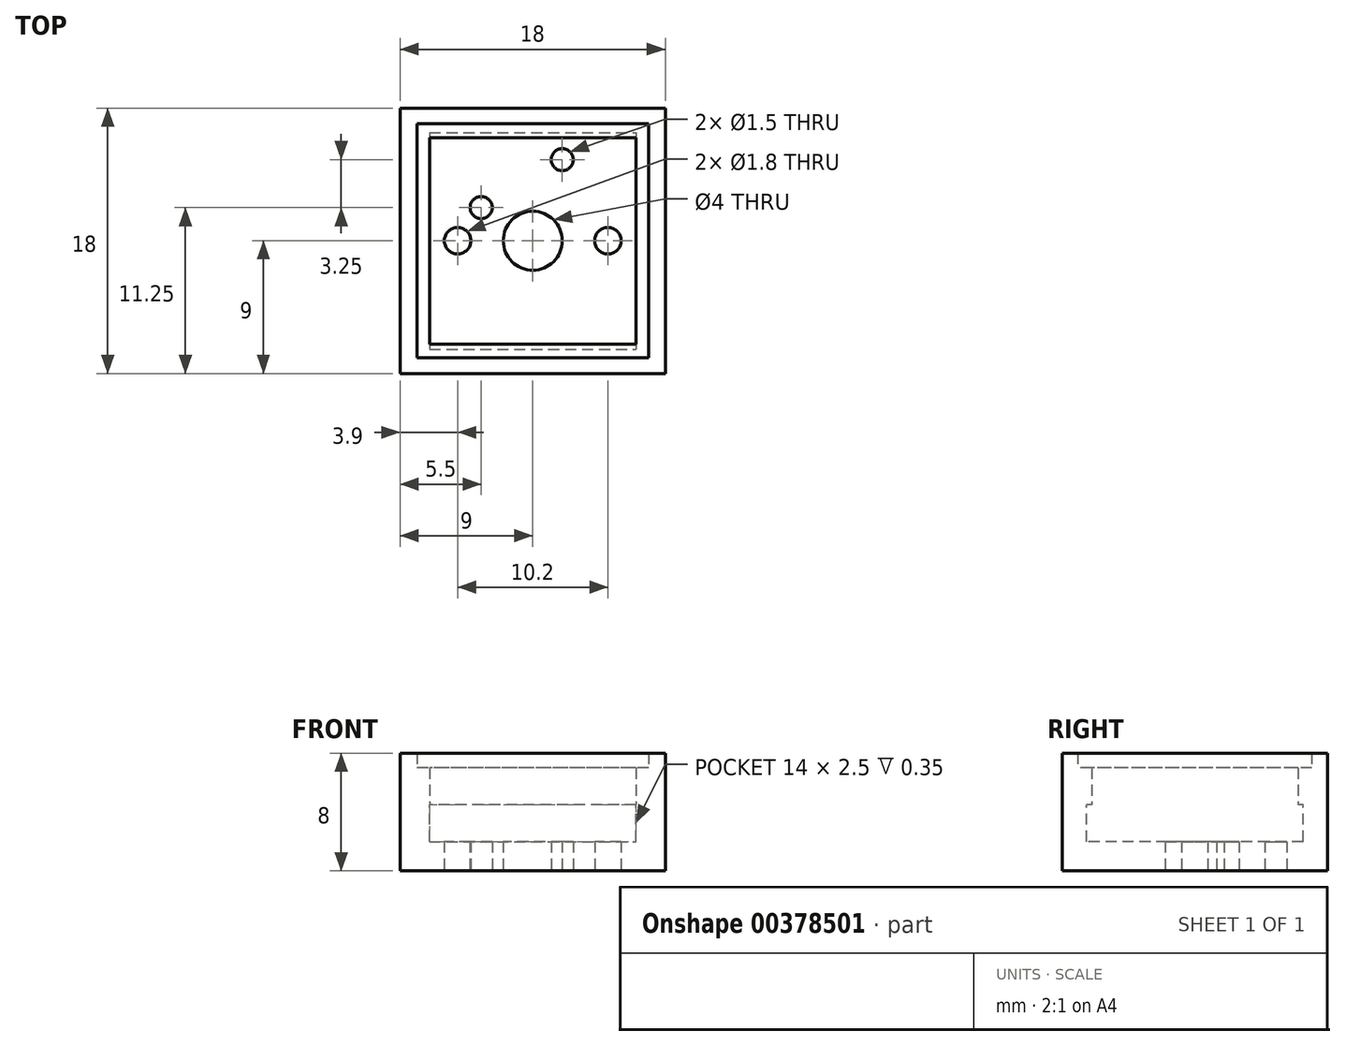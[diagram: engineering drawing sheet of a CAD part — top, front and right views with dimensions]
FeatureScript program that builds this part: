
annotation { "Feature Type Name" : "Feature", "Feature Type Description" : "" }
export const myFeature = defineFeature(function(context is Context, id is Id, definition is map)
    precondition{}
    {
        {
            var Q0;
            Q0=qCreatedBy(makeId("Top.planeOp"),FACE);
            var sketch = newSketch(context, id + "F0", { "sketchPlane" : qUnion([Q0])});
            skLineSegment(sketch, "E0.bottom", {"start": v(9, 9) * mm, "end": v(-9, 9) * mm});
            skLineSegment(sketch, "E0.top", {"start": v(9, -9) * mm, "end": v(-9, -9) * mm});
            skLineSegment(sketch, "E0.left", {"start": v(9, 9) * mm, "end": v(9, -9) * mm});
            skLineSegment(sketch, "E0.right", {"start": v(-9, 9) * mm, "end": v(-9, -9) * mm});
            skPoint(sketch, "E0.middle", {"position": v(0, 0) * mm});
            skLineSegment(sketch, "E1.bottom", {"start": v(7.85, 7.95) * mm, "end": v(-7.85, 7.95) * mm});
            skLineSegment(sketch, "E1.top", {"start": v(7.85, -7.95) * mm, "end": v(-7.85, -7.95) * mm});
            skLineSegment(sketch, "E1.left", {"start": v(7.85, 7.95) * mm, "end": v(7.85, -7.95) * mm});
            skLineSegment(sketch, "E1.right", {"start": v(-7.85, 7.95) * mm, "end": v(-7.85, -7.95) * mm});
            skLineSegment(sketch, "E2.bottom", {"start": v(7, 7) * mm, "end": v(-7, 7) * mm});
            skLineSegment(sketch, "E2.top", {"start": v(7, -7) * mm, "end": v(-7, -7) * mm});
            skLineSegment(sketch, "E2.left", {"start": v(7, 7) * mm, "end": v(7, -7) * mm});
            skLineSegment(sketch, "E2.right", {"start": v(-7, 7) * mm, "end": v(-7, -7) * mm});
            skLineSegment(sketch, "E3", {"start": v(-7, 0) * mm, "end": v(7, 0) * mm, "construction": true});
            skCircle(sketch, "E4", {"center": v(0, 0) * mm, "radius": 2 * mm});
            skLineSegment(sketch, "E5", {"start": v(0, 7) * mm, "end": v(0, -7) * mm, "construction": true});
            skCircle(sketch, "E6", {"center": v(-5.1, 0) * mm, "radius": 0.9 * mm});
            skCircle(sketch, "E7", {"center": v(5.1, 0) * mm, "radius": 0.9 * mm});
            skCircle(sketch, "E8", {"center": v(2, 5.5) * mm, "radius": 0.75 * mm});
            skCircle(sketch, "E9", {"center": v(-3.5, 2.25) * mm, "radius": 0.75 * mm});
            skSolve(sketch);
        }
        {
            var Q0;
            Q0=makeQuery(id+"F0.imprint","IMPRINT",FACE,{"disambiguationData":[TD([[makeQuery(id+"F0.imprint","IMPRINT",EDGE,{"derivedFrom":sQuery(id+"F0.wireOp",EDGE,"E2.bottom")}),1.0]])]});
            extrude(context, id + "F1", {"entities" : qUnion([Q0]), "depth" : 2 * mm});
        }
        {
            var Q0;
            Q0=qCreatedBy(makeId("Top.planeOp"),FACE);
            cPlane(context, id + "F2", {"entities" : qUnion([Q0]), "cplaneType" : CPlaneType.OFFSET, "offset" : 4.5 * mm, "width" : 150 * mm, "height" : 150 * mm});
        }
        {
            var Q0;
            Q0=makeQuery(id+"F0.imprint","IMPRINT",FACE,{"disambiguationData":[TD([[makeQuery(id+"F0.imprint","IMPRINT",EDGE,{"derivedFrom":sQuery(id+"F0.wireOp",EDGE,"E1.bottom")}),1.0]])]});
            extrude(context, id + "F3", {"entities" : qUnion([Q0]), "operationType" : NewBodyOperationType.ADD, "depth" : 7 * mm});
        }
        {
            var Q0;
            Q0=makeQuery(id+"F0.imprint","IMPRINT",FACE,{"disambiguationData":[TD([[makeQuery(id+"F0.imprint","IMPRINT",EDGE,{"derivedFrom":sQuery(id+"F0.wireOp",EDGE,"E0.bottom")}),1.0]])]});
            extrude(context, id + "F4", {"entities" : qUnion([Q0]), "operationType" : NewBodyOperationType.ADD, "depth" : 8 * mm});
        }
        {
            var Q0;
            Q0=qCreatedBy(id+"F2.planeOp",FACE);
            var sketch = newSketch(context, id + "F5", { "sketchPlane" : qUnion([Q0])});
            skLineSegment(sketch, "E10.bottom", {"start": v(7, 7.35) * mm, "end": v(-7, 7.35) * mm});
            skLineSegment(sketch, "E10.top", {"start": v(7, -7.35) * mm, "end": v(-7, -7.35) * mm});
            skLineSegment(sketch, "E10.left", {"start": v(7, 7.35) * mm, "end": v(7, -7.35) * mm});
            skLineSegment(sketch, "E10.right", {"start": v(-7, 7.35) * mm, "end": v(-7, -7.35) * mm});
            skPoint(sketch, "E10.middle", {"position": v(0, 0) * mm});
            skSolve(sketch);
        }
        {
            var Q0;
            Q0=qSketchRegion(id+"F5",true);
            var Q1;
            Q1=makeQuery(id+"F1.opExtrude","CAP_FACE",FACE,{"disambiguationData":[OSD([sQuery(id+"F0.wireOp",EDGE,"E2.bottom"),sQuery(id+"F0.wireOp",EDGE,"E2.top"),sQuery(id+"F0.wireOp",EDGE,"E2.left"),sQuery(id+"F0.wireOp",EDGE,"E2.right"),sQuery(id+"F0.wireOp",EDGE,"E4"),sQuery(id+"F0.wireOp",EDGE,"E6"),sQuery(id+"F0.wireOp",EDGE,"E7"),sQuery(id+"F0.wireOp",EDGE,"E8"),sQuery(id+"F0.wireOp",EDGE,"E9")])],"isStart":false});
            extrude(context, id + "F6", {"entities" : qUnion([Q0]), "operationType" : NewBodyOperationType.REMOVE, "endBound" : BoundingType.UP_TO_SURFACE, "oppositeDirection" : true, "endBoundEntityFace" : qUnion([Q1]), "depth" : 25 * mm});
        }
    });
